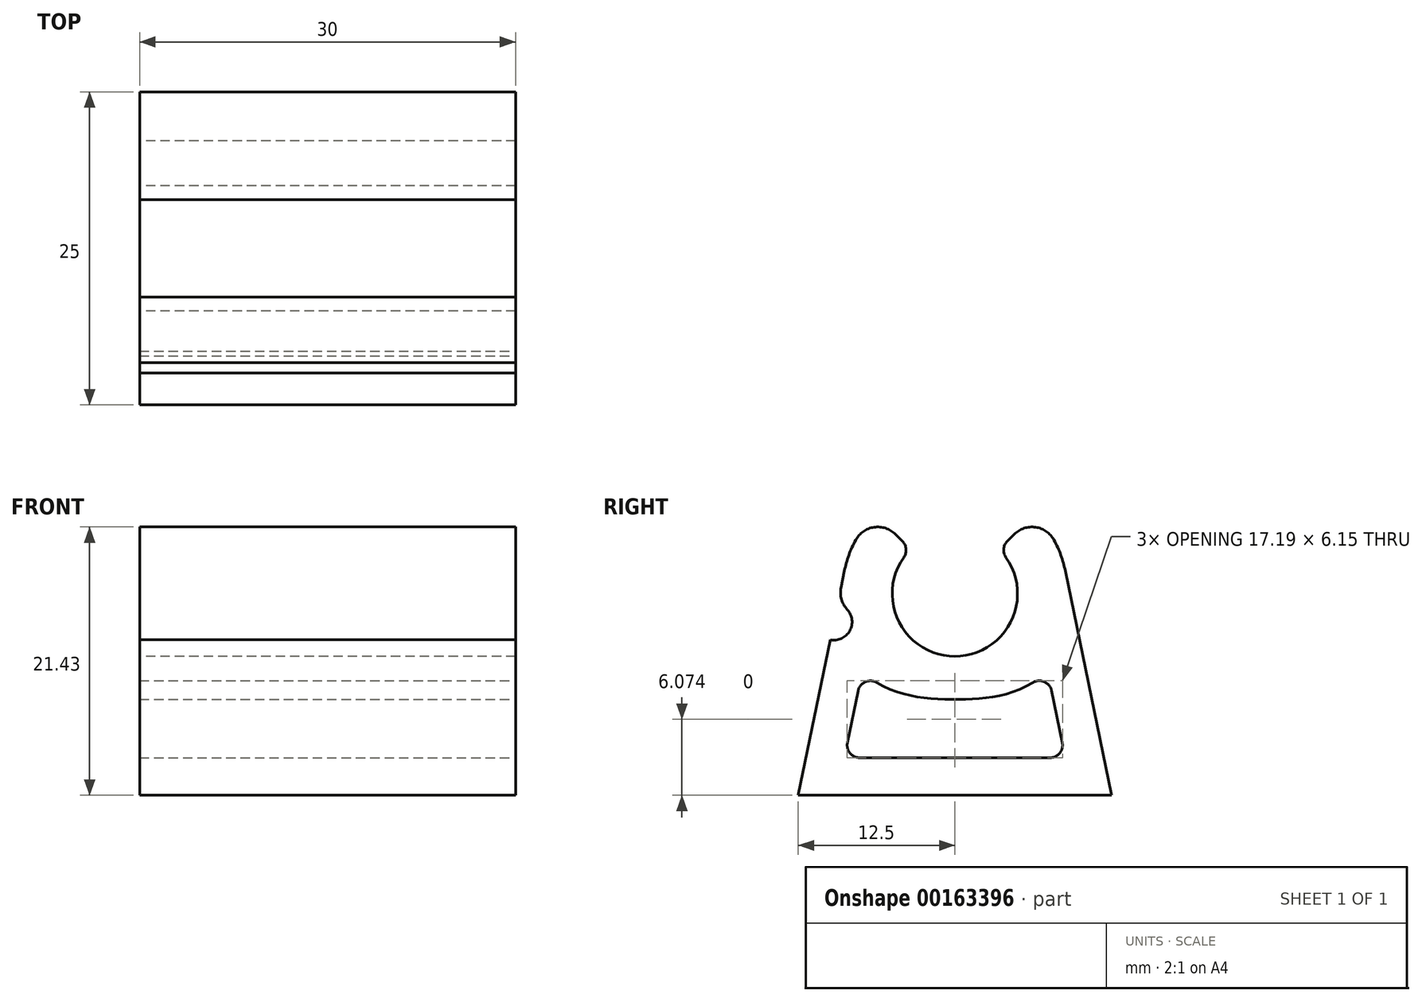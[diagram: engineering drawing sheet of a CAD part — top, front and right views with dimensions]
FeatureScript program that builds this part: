
annotation { "Feature Type Name" : "Feature", "Feature Type Description" : "" }
export const myFeature = defineFeature(function(context is Context, id is Id, definition is map)
    precondition{}
    {
        {
            var Q0;
            Q0=qCreatedBy(makeId("Right.planeOp"),FACE);
            var sketch = newSketch(context, id + "F0", { "sketchPlane" : qUnion([Q0])});
            skArc(sketch, "E0", {"start": v(-16.04, 39.64) * mm, "mid": v(-12.5, 31.1) * mm, "end": v(-8.96, 39.64) * mm});
            skArc(sketch, "E1", {"start": v(-3.68, 37.92) * mm, "mid": v(-4.58, 40.37) * mm, "end": v(-6.14, 42.47) * mm});
            skLineSegment(sketch, "E2", {"start": v(0, 20) * mm, "end": v(-3.68, 37.92) * mm});
            skLineSegment(sketch, "E3", {"start": v(-25, 20) * mm, "end": v(-21.32, 37.92) * mm});
            skLineSegment(sketch, "E4", {"start": v(0, 20) * mm, "end": v(-25, 20) * mm});
            skLineSegment(sketch, "E5", {"start": v(-8.96, 39.64) * mm, "end": v(-6.14, 42.47) * mm});
            skLineSegment(sketch, "E6", {"start": v(-16.04, 39.64) * mm, "end": v(-18.86, 42.47) * mm});
            skArc(sketch, "E7.trimOffspring", {"start": v(-18.86, 42.47) * mm, "mid": v(-20.42, 40.37) * mm, "end": v(-21.32, 37.92) * mm});
            skSolve(sketch);
        }
        {
            var Q0;
            Q0 = qSketchRegion(id + "F0", true);
            extrude(context, id + "F1", {"entities" : qUnion([Q0]), "depth" : 30 * mm});
        }
        {
            var Q0;
            Q0=makeQuery(id+"F1.opExtrude","SWEPT_EDGE",EDGE,{"disambiguationData":[OSD([sQuery(id+"F0.wireOp",EDGE,"E0"),sQuery(id+"F0.wireOp",EDGE,"E5")])]});
            var Q1;
            Q1=makeQuery(id+"F1.opExtrude","SWEPT_EDGE",EDGE,{"disambiguationData":[OSD([sQuery(id+"F0.wireOp",EDGE,"E0"),sQuery(id+"F0.wireOp",EDGE,"E6")])]});
            fillet(context, id + "F2", {"entities" : qUnion([Q0, Q1]), "radius" : 1 * mm, "tangentPropagation" : true, "allowEdgeOverflow" : false});
        }
        {
            var Q0;
            Q0=makeQuery(id+"F1.opExtrude","SWEPT_EDGE",EDGE,{"disambiguationData":[OSD([sQuery(id+"F0.wireOp",EDGE,"E1"),sQuery(id+"F0.wireOp",EDGE,"E5")])]});
            var Q1;
            Q1=makeQuery(id+"F1.opExtrude","SWEPT_EDGE",EDGE,{"disambiguationData":[OSD([sQuery(id+"F0.wireOp",EDGE,"E6"),sQuery(id+"F0.wireOp",EDGE,"E7.trimOffspring")])]});
            fillet(context, id + "F3", {"entities" : qUnion([Q0, Q1]), "radius" : 2 * mm, "tangentPropagation" : true, "allowEdgeOverflow" : false});
        }
        {
            var Q0;
            Q0=makeQuery(id+"F1.opExtrude","CAP_FACE",FACE,{"disambiguationData":[OSD([sQuery(id+"F0.wireOp",EDGE,"E0"),sQuery(id+"F0.wireOp",EDGE,"E1"),sQuery(id+"F0.wireOp",EDGE,"E2"),sQuery(id+"F0.wireOp",EDGE,"E3"),sQuery(id+"F0.wireOp",EDGE,"E4"),sQuery(id+"F0.wireOp",EDGE,"E5"),sQuery(id+"F0.wireOp",EDGE,"E6"),sQuery(id+"F0.wireOp",EDGE,"E7.trimOffspring")])],"isStart":false});
            var sketch = newSketch(context, id + "F4", { "sketchPlane" : qUnion([Q0])});
            skLineSegment(sketch, "E8", {"start": v(-21.32, 23) * mm, "end": v(-3.68, 23) * mm});
            skLineSegment(sketch, "E9", {"start": v(-3.68, 23) * mm, "end": v(-5.09, 29.86) * mm});
            skLineSegment(sketch, "E10", {"start": v(-21.32, 23) * mm, "end": v(-19.91, 29.86) * mm});
            skFitSpline(sketch, "E11", {"points": [v(-19.91, 29.86) * mm, v(-12.5, 27.66) * mm, v(-5.09, 29.86) * mm], "startDerivative": vector(13.78, -11.87) * mm, "endDerivative": vector(14.38, 12.06) * mm});
            skSolve(sketch);
        }
        {
            var Q0;
            Q0=makeQuery(id+"F4.imprint","IMPRINT",FACE,{"disambiguationData":[TD([[makeQuery(id+"F4.imprint","IMPRINT",EDGE,{"derivedFrom":sQuery(id+"F4.wireOp",EDGE,"E8")}),1.0]])]});
            extrude(context, id + "F5", {"entities" : qUnion([Q0]), "operationType" : NewBodyOperationType.REMOVE, "endBound" : BoundingType.UP_TO_NEXT, "oppositeDirection" : true, "depth" : 25 * mm});
        }
        {
            var Q0;
            Q0=makeQuery(id+"F5.boolean.opBoolean","COPY",EDGE,{"derivedFrom":makeQuery(id+"F5.opExtrude","SWEPT_EDGE",EDGE,{"disambiguationData":[OSD([sQuery(id+"F4.wireOp",EDGE,"E8"),sQuery(id+"F4.wireOp",EDGE,"E10")])]})});
            var Q1;
            Q1=makeQuery(id+"F5.boolean.opBoolean","COPY",EDGE,{"derivedFrom":makeQuery(id+"F5.opExtrude","SWEPT_EDGE",EDGE,{"disambiguationData":[OSD([sQuery(id+"F4.wireOp",EDGE,"E10"),sQuery(id+"F4.wireOp",EDGE,"E11")])]})});
            var Q2;
            Q2=makeQuery(id+"F5.boolean.opBoolean","COPY",EDGE,{"derivedFrom":makeQuery(id+"F5.opExtrude","SWEPT_EDGE",EDGE,{"disambiguationData":[OSD([sQuery(id+"F4.wireOp",EDGE,"E8"),sQuery(id+"F4.wireOp",EDGE,"E9")])]})});
            var Q3;
            Q3=makeQuery(id+"F5.boolean.opBoolean","COPY",EDGE,{"derivedFrom":makeQuery(id+"F5.opExtrude","SWEPT_EDGE",EDGE,{"disambiguationData":[OSD([sQuery(id+"F4.wireOp",EDGE,"E9"),sQuery(id+"F4.wireOp",EDGE,"E11")])]})});
            fillet(context, id + "F6", {"entities" : qUnion([Q0, Q1, Q2, Q3]), "radius" : 1 * mm, "tangentPropagation" : true, "allowEdgeOverflow" : false});
        }
        {
            var Q0;
            Q0=makeQuery(id+"F1.opExtrude","CAP_FACE",FACE,{"disambiguationData":[OSD([sQuery(id+"F0.wireOp",EDGE,"E0"),sQuery(id+"F0.wireOp",EDGE,"E1"),sQuery(id+"F0.wireOp",EDGE,"E2"),sQuery(id+"F0.wireOp",EDGE,"E3"),sQuery(id+"F0.wireOp",EDGE,"E4"),sQuery(id+"F0.wireOp",EDGE,"E5"),sQuery(id+"F0.wireOp",EDGE,"E6"),sQuery(id+"F0.wireOp",EDGE,"E7.trimOffspring")])],"isStart":false});
            var sketch = newSketch(context, id + "F7", { "sketchPlane" : qUnion([Q0])});
            skCircle(sketch, "E12", {"center": v(-22.15, 33.85) * mm, "radius": 1.45 * mm});
            skCircle(sketch, "E13.MirrorC", {"center": v(-2.85, 33.85) * mm, "radius": 1.45 * mm});
            skSolve(sketch);
        }
        {
            var Q0;
            {var subQ0=sQuery(id+"F7.wireOp",EDGE,"E13.MirrorC");var subQ1=makeQuery(id+"F1.opExtrude","CAP_EDGE",EDGE,{"disambiguationData":[OSD([sQuery(id+"F0.wireOp",EDGE,"E2")])],"isStart":false});var subQ2=makeQuery(id+"F7.imprint","INTERSECT",VERTEX,{"disambiguationData":[OD(0.0)],"derivedFrom":[subQ1,subQ0]});Q0=makeQuery(id+"F7.imprint","IMPRINT",FACE,{"disambiguationData":[TD([[makeQuery(id+"F7.imprint","IMPRINT",EDGE,{"disambiguationData":[TD([[subQ2,1.0]])],"derivedFrom":subQ0}),-1.0]])]});}
            var Q1;
            {var subQ0=sQuery(id+"F7.wireOp",EDGE,"E12");var subQ1=makeQuery(id+"F1.opExtrude","CAP_EDGE",EDGE,{"disambiguationData":[OSD([sQuery(id+"F0.wireOp",EDGE,"E3")])],"isStart":false});var subQ2=makeQuery(id+"F7.imprint","INTERSECT",VERTEX,{"disambiguationData":[OD(0.0)],"derivedFrom":[subQ1,subQ0]});Q1=makeQuery(id+"F7.imprint","IMPRINT",FACE,{"disambiguationData":[TD([[makeQuery(id+"F7.imprint","IMPRINT",EDGE,{"disambiguationData":[TD([[subQ2,-1.0]])],"derivedFrom":subQ0}),1.0]])]});}
            extrude(context, id + "F8", {"entities" : qUnion([Q0, Q1]), "operationType" : NewBodyOperationType.REMOVE, "endBound" : BoundingType.UP_TO_NEXT, "oppositeDirection" : true, "depth" : 25 * mm});
        }
        {
            var Q0;
            {var subQ0=sQuery(id+"F7.wireOp",EDGE,"E12");var subQ1=sQuery(id+"F0.wireOp",EDGE,"E3");Q0=makeQuery(id+"F8.boolean.opBoolean","COPY",EDGE,{"derivedFrom":makeQuery(id+"F8.opExtrude","SWEPT_EDGE",EDGE,{"disambiguationData":[OSD([subQ1,subQ0]),TDD([makeQuery(id+"F7.imprint","INTERSECT",VERTEX,{"disambiguationData":[OD(1.0)],"derivedFrom":[makeQuery(id+"F1.opExtrude","CAP_EDGE",EDGE,{"disambiguationData":[OSD([subQ1])],"isStart":false}),subQ0]})])]})});}
            var Q1;
            {var subQ0=sQuery(id+"F7.wireOp",EDGE,"E12");var subQ1=sQuery(id+"F0.wireOp",EDGE,"E3");Q1=makeQuery(id+"F8.boolean.opBoolean","COPY",EDGE,{"derivedFrom":makeQuery(id+"F8.opExtrude","SWEPT_EDGE",EDGE,{"disambiguationData":[OSD([subQ1,subQ0]),TDD([makeQuery(id+"F7.imprint","INTERSECT",VERTEX,{"disambiguationData":[OD(0.0)],"derivedFrom":[makeQuery(id+"F1.opExtrude","CAP_EDGE",EDGE,{"disambiguationData":[OSD([subQ1])],"isStart":false}),subQ0]})])]})});}
            var Q2;
            {var subQ0=sQuery(id+"F7.wireOp",EDGE,"E13.MirrorC");var subQ1=sQuery(id+"F0.wireOp",EDGE,"E2");Q2=makeQuery(id+"F8.boolean.opBoolean","COPY",EDGE,{"derivedFrom":makeQuery(id+"F8.opExtrude","SWEPT_EDGE",EDGE,{"disambiguationData":[OSD([subQ1,subQ0]),TDD([makeQuery(id+"F7.imprint","INTERSECT",VERTEX,{"disambiguationData":[OD(0.0)],"derivedFrom":[makeQuery(id+"F1.opExtrude","CAP_EDGE",EDGE,{"disambiguationData":[OSD([subQ1])],"isStart":false}),subQ0]})])]})});}
            var Q3;
            {var subQ0=sQuery(id+"F7.wireOp",EDGE,"E13.MirrorC");var subQ1=sQuery(id+"F0.wireOp",EDGE,"E2");Q3=makeQuery(id+"F8.boolean.opBoolean","COPY",EDGE,{"derivedFrom":makeQuery(id+"F8.opExtrude","SWEPT_EDGE",EDGE,{"disambiguationData":[OSD([subQ1,subQ0]),TDD([makeQuery(id+"F7.imprint","INTERSECT",VERTEX,{"disambiguationData":[OD(1.0)],"derivedFrom":[makeQuery(id+"F1.opExtrude","CAP_EDGE",EDGE,{"disambiguationData":[OSD([subQ1])],"isStart":false}),subQ0]})])]})});}
            fillet(context, id + "F9", {"entities" : qUnion([Q0, Q1, Q2, Q3]), "radius" : 2 * mm, "tangentPropagation" : true, "allowEdgeOverflow" : false});
        }
    });
